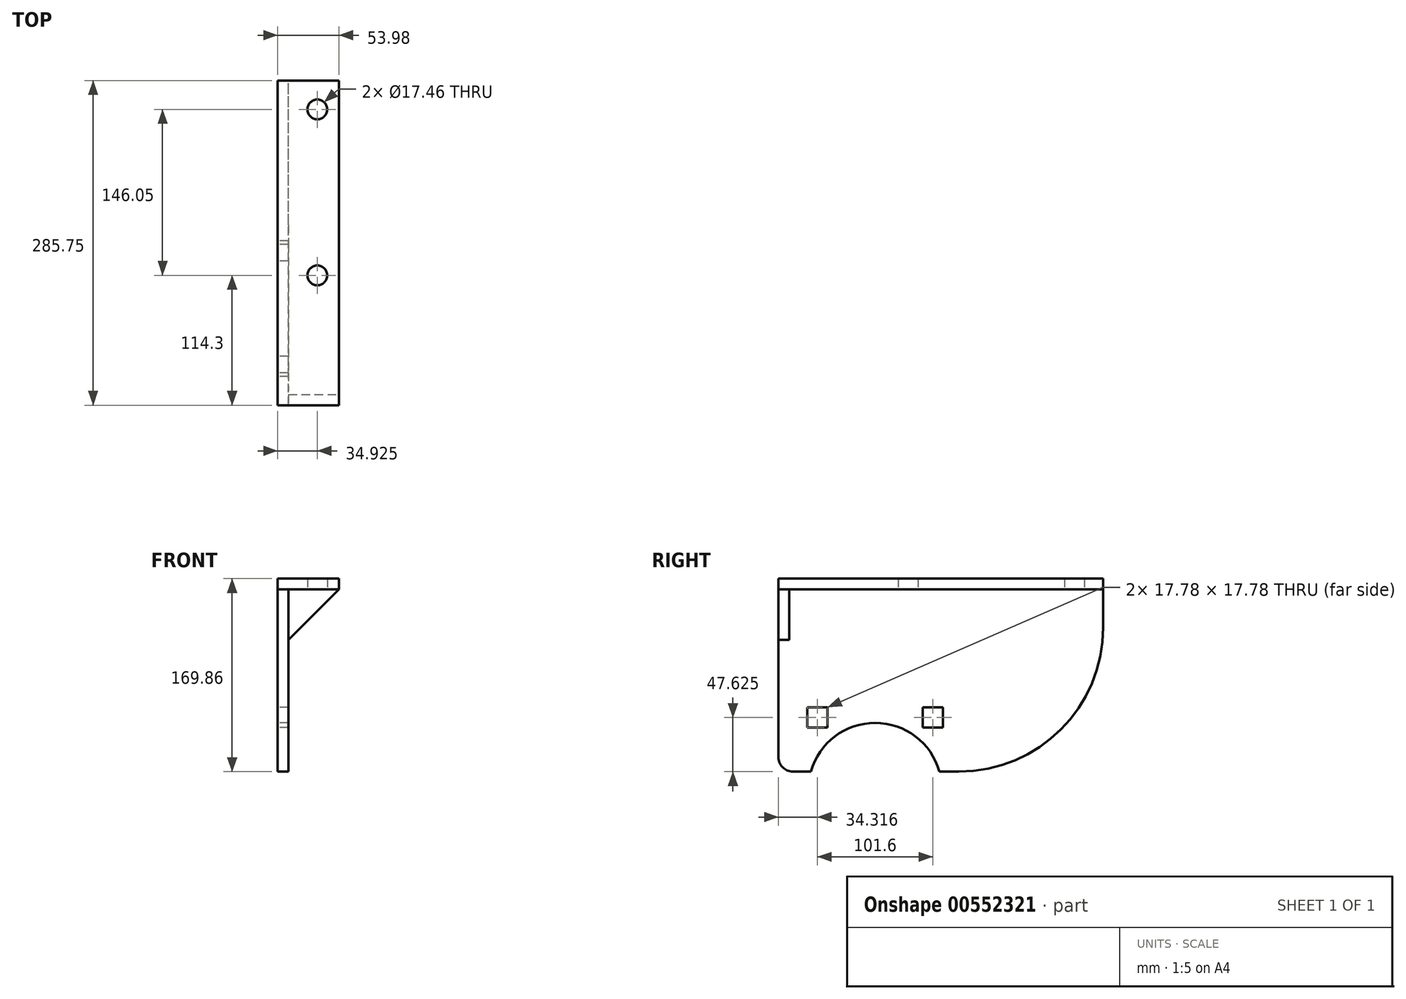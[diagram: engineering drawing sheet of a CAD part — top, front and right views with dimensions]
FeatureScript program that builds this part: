
annotation { "Feature Type Name" : "Feature", "Feature Type Description" : "" }
export const myFeature = defineFeature(function(context is Context, id is Id, definition is map)
    precondition{}
    {
        {
            var Q0;
            Q0=qCreatedBy(makeId("Right.planeOp"),FACE);
            var sketch = newSketch(context, id + "F0", { "sketchPlane" : qUnion([Q0])});
            skLineSegment(sketch, "E0", {"start": v(0, 12.7) * mm, "end": v(0, 160.34) * mm});
            skLineSegment(sketch, "E1", {"start": v(0, 160.34) * mm, "end": v(285.75, 160.34) * mm});
            skLineSegment(sketch, "E2", {"start": v(285.75, 160.34) * mm, "end": v(285.75, 127) * mm});
            skLineSegment(sketch, "E3", {"start": v(158.75, 0) * mm, "end": v(141.66, 0) * mm});
            skCircle(sketch, "E4", {"center": v(85.12, -15.91) * mm, "radius": 74.61 * mm, "construction": true});
            skArc(sketch, "E5", {"start": v(141.66, 0) * mm, "mid": v(85.12, 42.82) * mm, "end": v(28.57, 0) * mm});
            skLineSegment(sketch, "E6.bottom", {"start": v(25.43, 56.52) * mm, "end": v(43.2, 56.52) * mm});
            skLineSegment(sketch, "E6.top", {"start": v(25.43, 38.74) * mm, "end": v(43.2, 38.74) * mm});
            skLineSegment(sketch, "E6.left", {"start": v(25.43, 56.52) * mm, "end": v(25.43, 38.74) * mm});
            skLineSegment(sketch, "E6.right", {"start": v(43.2, 56.52) * mm, "end": v(43.2, 38.74) * mm});
            skLineSegment(sketch, "E7.bottom", {"start": v(127.03, 56.52) * mm, "end": v(144.8, 56.52) * mm});
            skLineSegment(sketch, "E7.top", {"start": v(127.03, 38.74) * mm, "end": v(144.8, 38.74) * mm});
            skLineSegment(sketch, "E7.left", {"start": v(127.03, 56.52) * mm, "end": v(127.03, 38.74) * mm});
            skLineSegment(sketch, "E7.right", {"start": v(144.8, 56.52) * mm, "end": v(144.8, 38.74) * mm});
            skLineSegment(sketch, "E8", {"start": v(25.43, 47.63) * mm, "end": v(144.8, 47.63) * mm, "construction": true});
            skLineSegment(sketch, "E9", {"start": v(34.32, 56.52) * mm, "end": v(34.32, 38.74) * mm, "construction": true});
            skLineSegment(sketch, "E10", {"start": v(135.92, 56.52) * mm, "end": v(135.92, 38.74) * mm, "construction": true});
            skLineSegment(sketch, "E11.trimOffspring", {"start": v(28.58, 0) * mm, "end": v(12.7, 0) * mm});
            skPoint(sketch, "E12.visualSharp", {"position": v(0, 0) * mm});
            skArc(sketch, "E12.filletArc", {"start": v(0, 12.7) * mm, "mid": v(3.72, 3.72) * mm, "end": v(12.7, 0) * mm});
            skPoint(sketch, "E13.visualSharp", {"position": v(285.75, 0) * mm});
            skArc(sketch, "E13.filletArc", {"start": v(158.75, 0) * mm, "mid": v(248.55, 37.2) * mm, "end": v(285.75, 127) * mm});
            skSolve(sketch);
        }
        {
            var Q0;
            Q0 = qSketchRegion(id + "F0", true);
            extrude(context, id + "F1", {"entities" : qUnion([Q0]), "depth" : 9.52 * mm, "offsetDistance" : 25.4 * mm});
        }
        {
            var Q0;
            Q0=makeQuery(id+"F1.opExtrude","SWEPT_FACE",FACE,{"disambiguationData":[OSD([sQuery(id+"F0.wireOp",EDGE,"E1")])]});
            var sketch = newSketch(context, id + "F2", { "sketchPlane" : qUnion([Q0])});
            skPoint(sketch, "E14.oppositeSnap0", {"position": v(53.97, 0) * mm});
            skLineSegment(sketch, "E14.bottom", {"start": v(0, 0) * mm, "end": v(53.97, 0) * mm});
            skLineSegment(sketch, "E14.top", {"start": v(0, 285.75) * mm, "end": v(53.97, 285.75) * mm});
            skLineSegment(sketch, "E14.left", {"start": v(0, 0) * mm, "end": v(0, 285.75) * mm});
            skLineSegment(sketch, "E14.right", {"start": v(53.97, 0) * mm, "end": v(53.97, 285.75) * mm});
            skCircle(sketch, "E15", {"center": v(34.92, 260.35) * mm, "radius": 8.73 * mm});
            skCircle(sketch, "E16", {"center": v(34.92, 114.3) * mm, "radius": 8.73 * mm});
            skLineSegment(sketch, "E17", {"start": v(34.92, 260.35) * mm, "end": v(34.92, 114.3) * mm, "construction": true});
            skSolve(sketch);
        }
        {
            var Q0;
            Q0 = qSketchRegion(id + "F2", true);
            extrude(context, id + "F3", {"entities" : qUnion([Q0]), "depth" : 9.52 * mm, "offsetDistance" : 25.4 * mm});
        }
        {
            var Q0;
            Q0=makeQuery(id+"F1.opExtrude","SWEPT_FACE",FACE,{"disambiguationData":[OSD([sQuery(id+"F0.wireOp",EDGE,"E0")])]});
            var sketch = newSketch(context, id + "F4", { "sketchPlane" : qUnion([Q0])});
            skLineSegment(sketch, "E18", {"start": v(9.52, 115.89) * mm, "end": v(53.97, 160.34) * mm});
            skLineSegment(sketch, "E19", {"start": v(53.97, 160.34) * mm, "end": v(9.52, 160.34) * mm});
            skLineSegment(sketch, "E20", {"start": v(9.52, 160.34) * mm, "end": v(9.53, 115.89) * mm});
            skSolve(sketch);
        }
        {
            var Q0;
            Q0 = qSketchRegion(id + "F4", true);
            extrude(context, id + "F5", {"entities" : qUnion([Q0]), "oppositeDirection" : true, "depth" : 9.52 * mm, "offsetDistance" : 25.4 * mm});
        }
    });
